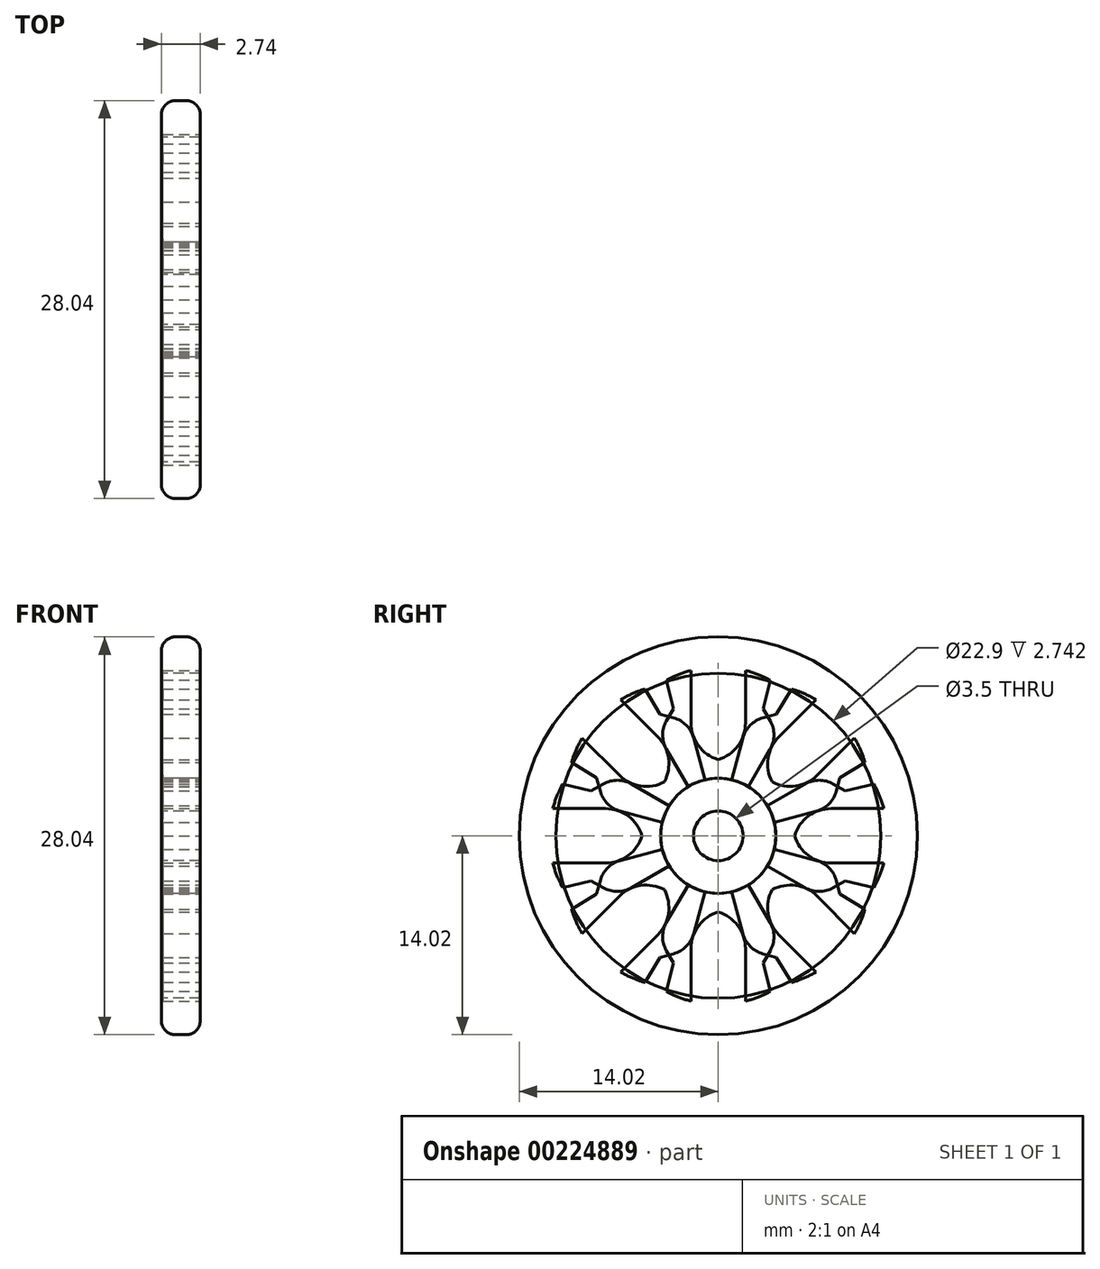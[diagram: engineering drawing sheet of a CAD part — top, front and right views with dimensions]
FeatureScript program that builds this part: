
annotation { "Feature Type Name" : "Feature", "Feature Type Description" : "" }
export const myFeature = defineFeature(function(context is Context, id is Id, definition is map)
    precondition{}
    {
        {
            var Q0;
            Q0=qCreatedBy(makeId("Top.planeOp"),FACE);
            var sketch = newSketch(context, id + "F0", { "sketchPlane" : qUnion([Q0])});
            skLineSegment(sketch, "E0", {"start": v(0, 14.02) * mm, "end": v(2.74, 14.02) * mm});
            skLineSegment(sketch, "E1", {"start": v(2.74, 14.02) * mm, "end": v(2.74, 11.45) * mm});
            skLineSegment(sketch, "E2", {"start": v(2.74, 11.45) * mm, "end": v(0, 11.45) * mm});
            skLineSegment(sketch, "E3", {"start": v(0, 1.75) * mm, "end": v(2.74, 1.75) * mm});
            skLineSegment(sketch, "E4", {"start": v(2.74, 1.75) * mm, "end": v(2.74, 4.06) * mm});
            skLineSegment(sketch, "E5", {"start": v(2.74, 4.06) * mm, "end": v(0, 4.06) * mm});
            skLineSegment(sketch, "E6", {"start": v(0, 11.45) * mm, "end": v(0, 14.02) * mm});
            skLineSegment(sketch, "E7", {"start": v(0, 1.75) * mm, "end": v(0, 4.06) * mm});
            skLineSegment(sketch, "E8", {"start": v(-18.73, 0) * mm, "end": v(12.6, 0) * mm, "construction": true});
            skSolve(sketch);
        }
        {
            var Q0;
            Q0=makeQuery(id+"F0.imprint","IMPRINT",FACE,{"disambiguationData":[TD([[makeQuery(id+"F0.imprint","IMPRINT",EDGE,{"derivedFrom":sQuery(id+"F0.wireOp",EDGE,"E0")}),-1.0]])]});
            var Q1;
            Q1=makeQuery(id+"F0.imprint","IMPRINT",FACE,{"disambiguationData":[TD([[makeQuery(id+"F0.imprint","IMPRINT",EDGE,{"derivedFrom":sQuery(id+"F0.wireOp",EDGE,"E3")}),1.0]])]});
            var Q2;
            Q2=sQuery(id+"F0.wireOp",EDGE,"E8");
            revolve(context, id + "F1", {"entities" : qUnion([Q0, Q1]), "axis" : qUnion([Q2]), "revolveType" : RevolveType.FULL});
        }
        {
            var Q0;
            Q0=makeQuery(id+"F1.opRevolve","SWEPT_FACE",FACE,{"disambiguationData":[OSD([sQuery(id+"F0.wireOp",EDGE,"E4")])]});
            var sketch = newSketch(context, id + "F2", { "sketchPlane" : qUnion([Q0])});
            skLineSegment(sketch, "E9", {"start": v(-1.1, 1.7) * mm, "end": v(-3.65, 6.1) * mm});
            skLineSegment(sketch, "E10", {"start": v(-1.37, 12.11) * mm, "end": v(0, 12.11) * mm});
            skPoint(sketch, "E11.visualSharp", {"position": v(-4.22, 7.1) * mm});
            skArc(sketch, "E11.filletArc", {"start": v(-3.66, 8.1) * mm, "mid": v(-3.92, 7.1) * mm, "end": v(-3.65, 6.1) * mm});
            skLineSegment(sketch, "E12", {"start": v(-3.17, 8.96) * mm, "end": v(-3.66, 10.97) * mm});
            skLineSegment(sketch, "E13", {"start": v(-3.66, 8.1) * mm, "end": v(-3.17, 8.96) * mm});
            skFitSpline(sketch, "E14", {"points": [v(-3.66, 10.97) * mm, v(0, 11.6) * mm], "startDerivative": vector(2.03, 1.06) * mm, "endDerivative": vector(4.11, -1.54) * mm});
            skLineSegment(sketch, "E15.MirrorCS", {"start": v(3.66, 8.1) * mm, "end": v(3.17, 8.96) * mm});
            skArc(sketch, "E16.MirrorCS", {"start": v(3.66, 8.1) * mm, "mid": v(3.92, 7.1) * mm, "end": v(3.65, 6.1) * mm});
            skLineSegment(sketch, "E17.MirrorCS", {"start": v(1.1, 1.7) * mm, "end": v(3.65, 6.1) * mm});
            skLineSegment(sketch, "E18.MirrorCS", {"start": v(3.17, 8.96) * mm, "end": v(3.66, 10.97) * mm});
            skFitSpline(sketch, "E19.MirrorCS", {"points": [v(3.66, 10.97) * mm, v(0, 11.6) * mm], "startDerivative": vector(-2.03, 1.06) * mm, "endDerivative": vector(-4.11, -1.54) * mm});
            skLineSegment(sketch, "E20", {"start": v(-1.92, 7.95) * mm, "end": v(-1.92, 11.65) * mm});
            skArc(sketch, "E21", {"start": v(-1.92, 7.95) * mm, "mid": v(-1.39, 6.34) * mm, "end": v(0, 5.37) * mm});
            skArc(sketch, "E22.MirrorCS", {"start": v(1.92, 7.95) * mm, "mid": v(1.39, 6.34) * mm, "end": v(0, 5.37) * mm});
            skLineSegment(sketch, "E23.MirrorCS", {"start": v(1.92, 7.95) * mm, "end": v(1.92, 11.65) * mm});
            skSolve(sketch);
        }
        {
            var Q0;
            {var subQ4=sQuery(id+"F2.wireOp",EDGE,"E11.filletArc");Q0=makeQuery(id+"F2.imprint","IMPRINT",FACE,{"disambiguationData":[TD([[makeQuery(id+"F2.imprint","IMPRINT",EDGE,{"derivedFrom":subQ4}),1.0]])]});}
            extrude(context, id + "F3", {"entities" : qUnion([Q0]), "oppositeDirection" : true, "depth" : 2.65 * mm});
        }
        {
            var Q0;
            Q0=makeQuery(id+"F3.opExtrude","SWEPT_BODY",BODY,{"disambiguationData":[OSD([sQuery(id+"F0.wireOp",EDGE,"E4"),sQuery(id+"F0.wireOp",EDGE,"E5"),sQuery(id+"F2.wireOp",EDGE,"E9"),sQuery(id+"F2.wireOp",EDGE,"E11.filletArc"),sQuery(id+"F2.wireOp",EDGE,"8806c90a-8590-4166-91d8-616a10c64add"),sQuery(id+"F2.wireOp",EDGE,"E12"),sQuery(id+"F2.wireOp",EDGE,"E13"),sQuery(id+"F2.wireOp",EDGE,"E14"),sQuery(id+"F2.wireOp",EDGE,"E15.MirrorCS"),sQuery(id+"F2.wireOp",EDGE,"E16.MirrorCS"),sQuery(id+"F2.wireOp",EDGE,"E17.MirrorCS"),sQuery(id+"F2.wireOp",EDGE,"E18.MirrorCS"),sQuery(id+"F2.wireOp",EDGE,"E19.MirrorCS"),sQuery(id+"F2.wireOp",EDGE,"50fd80b4-de9e-4aac-b472-490e496855450.MirrorCS")])]});
            var Q1;
            Q1=makeQuery(id+"F1.opRevolve","SWEPT_EDGE",EDGE,{"disambiguationData":[OSD([sQuery(id+"F0.wireOp",EDGE,"E1"),sQuery(id+"F0.wireOp",EDGE,"E2")])]});
            circularPattern(context, id + "F4", {"entities" : qUnion([Q0]), "axis" : qUnion([Q1]), "angle" : 360 * degree, "instanceCount" : 8, "equalSpace" : true});
        }
        {
            var Q0;
            Q0=makeQuery(id+"F1.opRevolve","SWEPT_EDGE",EDGE,{"disambiguationData":[OSD([sQuery(id+"F0.wireOp",EDGE,"E0"),sQuery(id+"F0.wireOp",EDGE,"E6")])]});
            fillet(context, id + "F5", {"entities" : qUnion([Q0]), "radius" : 1 * mm, "tangentPropagation" : true, "allowEdgeOverflow" : false});
        }
        {
            var Q0;
            Q0=makeQuery(id+"F1.opRevolve","SWEPT_EDGE",EDGE,{"disambiguationData":[OSD([sQuery(id+"F0.wireOp",EDGE,"E0"),sQuery(id+"F0.wireOp",EDGE,"E1")])]});
            fillet(context, id + "F6", {"entities" : qUnion([Q0]), "radius" : 1 * mm, "tangentPropagation" : true, "allowEdgeOverflow" : false});
        }
    });
